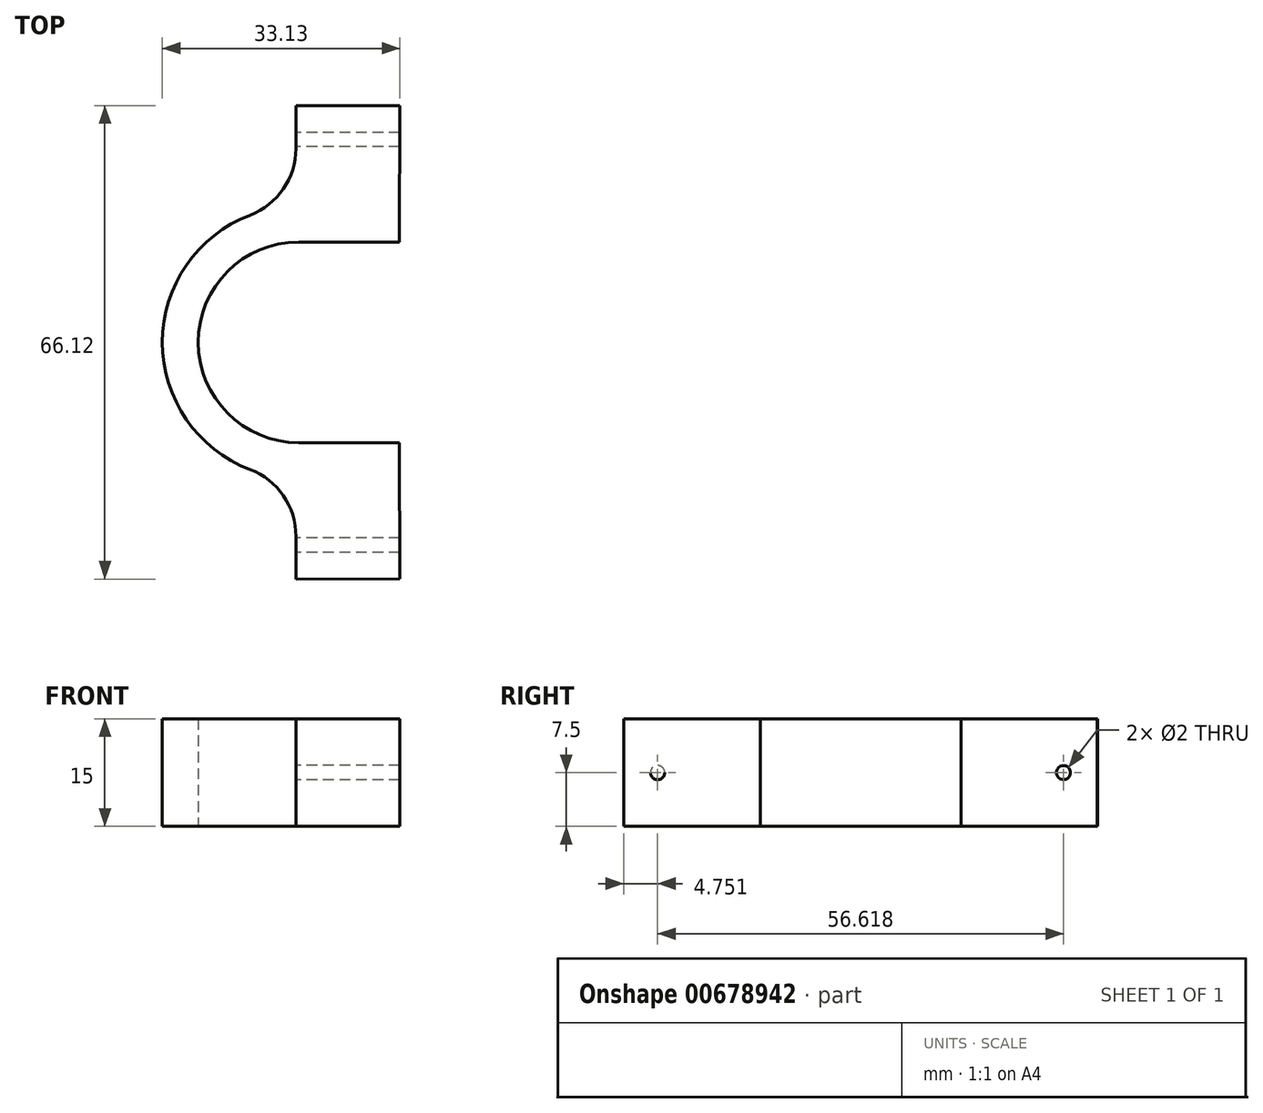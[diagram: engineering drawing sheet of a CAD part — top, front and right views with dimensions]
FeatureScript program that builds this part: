
annotation { "Feature Type Name" : "Feature", "Feature Type Description" : "" }
export const myFeature = defineFeature(function(context is Context, id is Id, definition is map)
    precondition{}
    {
        {
            var Q0;
            Q0=qCreatedBy(makeId("Top.planeOp"),FACE);
            var sketch = newSketch(context, id + "F0", { "sketchPlane" : qUnion([Q0])});
            skLineSegment(sketch, "E0.top", {"start": v(0, 0) * mm, "end": v(14, 0) * mm});
            skLineSegment(sketch, "E0.right", {"start": v(14.13, 33) * mm, "end": v(14.05, 14) * mm});
            skArc(sketch, "E1", {"start": v(0, 14) * mm, "mid": v(-9.9, 9.9) * mm, "end": v(-14, 0) * mm});
            skLineSegment(sketch, "E2.0", {"start": v(-0.36, 33.06) * mm, "end": v(-0.36, 19) * mm});
            skLineSegment(sketch, "E2.1", {"start": v(-0.36, 33.06) * mm, "end": v(14.13, 33) * mm});
            skArc(sketch, "E3.trimOffspring", {"start": v(-0.36, 19) * mm, "mid": v(-13.56, 13.3) * mm, "end": v(-19, 0) * mm});
            skLineSegment(sketch, "E4", {"start": v(0, 14) * mm, "end": v(14.05, 14) * mm});
            skLineSegment(sketch, "E5", {"start": v(0, 0) * mm, "end": v(-52.17, 0) * mm});
            skLineSegment(sketch, "E6.MirrorCS", {"start": v(0, -14) * mm, "end": v(14.05, -14) * mm});
            skArc(sketch, "E7.MirrorCS", {"start": v(0, -14) * mm, "mid": v(-9.9, -9.9) * mm, "end": v(-14, 0) * mm});
            skArc(sketch, "E8.MirrorCS", {"start": v(-0.36, -19) * mm, "mid": v(-13.56, -13.3) * mm, "end": v(-19, 0) * mm});
            skLineSegment(sketch, "E9.MirrorCS", {"start": v(-0.36, -33.06) * mm, "end": v(-0.36, -19) * mm});
            skLineSegment(sketch, "E10.MirrorCS", {"start": v(-0.36, -33.06) * mm, "end": v(14.13, -33) * mm});
            skLineSegment(sketch, "E11.MirrorCS", {"start": v(14.13, -33) * mm, "end": v(14.05, -14) * mm});
            skLineSegment(sketch, "E12", {"start": v(14.05, -14) * mm, "end": v(14, 0) * mm});
            skLineSegment(sketch, "E13", {"start": v(14.05, 14) * mm, "end": v(14, 0) * mm});
            skSolve(sketch);
        }
        {
            var Q0;
            Q0=makeQuery(id+"F0.imprint","IMPRINT",FACE,{"disambiguationData":[TD([[makeQuery(id+"F0.imprint","IMPRINT",EDGE,{"derivedFrom":sQuery(id+"F0.wireOp",EDGE,"E0.right")}),-1.0]])]});
            var Q1;
            Q1=makeQuery(id+"F0.imprint","IMPRINT",FACE,{"disambiguationData":[TD([[makeQuery(id+"F0.imprint","IMPRINT",EDGE,{"derivedFrom":sQuery(id+"F0.wireOp",EDGE,"E6.MirrorCS")}),-1.0]])]});
            extrude(context, id + "F1", {"entities" : qUnion([Q0, Q1]), "depth" : 15 * mm, "offsetDistance" : 25 * mm});
        }
        {
            var Q0;
            Q0=makeQuery(id+"F1.opExtrude","SWEPT_EDGE",EDGE,{"disambiguationData":[OSD([sQuery(id+"F0.wireOp",EDGE,"E2.0"),sQuery(id+"F0.wireOp",EDGE,"E3.trimOffspring")])]});
            var Q1;
            Q1=makeQuery(id+"F1.opExtrude","SWEPT_EDGE",EDGE,{"disambiguationData":[OSD([sQuery(id+"F0.wireOp",EDGE,"E8.MirrorCS"),sQuery(id+"F0.wireOp",EDGE,"E9.MirrorCS")])]});
            fillet(context, id + "F2", {"entities" : qUnion([Q0, Q1]), "radius" : 10 * mm, "tangentPropagation" : true, "allowEdgeOverflow" : false});
        }
        {
            var Q0;
            Q0=makeQuery(id+"F1.opExtrude","SWEPT_FACE",FACE,{"disambiguationData":[OSD([sQuery(id+"F0.wireOp",EDGE,"E2.0")])]});
            var sketch = newSketch(context, id + "F3", { "sketchPlane" : qUnion([Q0])});
            skPoint(sketch, "E14", {"position": v(-28.3, 7.5) * mm});
            skPoint(sketch, "E14.positionSnap0", {"position": v(-33.06, 7.5) * mm});
            skLineSegment(sketch, "E15", {"start": v(0, 0) * mm, "end": v(0, 9.4) * mm});
            skPoint(sketch, "E16.MirrorP", {"position": v(28.3, 7.5) * mm});
            skSolve(sketch);
        }
        {
            var Q0;
            Q0=sQuery(id+"F3.wireOp",VERTEX,"E14");
            var Q1;
            Q1=sQuery(id+"F3.wireOp",VERTEX,"E16.MirrorP");
            var Q2;
            Q2=makeQuery(id+"F1.opExtrude","SWEPT_BODY",BODY,{"disambiguationData":[OSD([sQuery(id+"F0.wireOp",EDGE,"E0.right"),sQuery(id+"F0.wireOp",EDGE,"E1"),sQuery(id+"F0.wireOp",EDGE,"E2.0"),sQuery(id+"F0.wireOp",EDGE,"E2.1"),sQuery(id+"F0.wireOp",EDGE,"E3.trimOffspring"),sQuery(id+"F0.wireOp",EDGE,"E4"),sQuery(id+"F0.wireOp",EDGE,"E6.MirrorCS"),sQuery(id+"F0.wireOp",EDGE,"E7.MirrorCS"),sQuery(id+"F0.wireOp",EDGE,"E8.MirrorCS"),sQuery(id+"F0.wireOp",EDGE,"E9.MirrorCS"),sQuery(id+"F0.wireOp",EDGE,"E10.MirrorCS"),sQuery(id+"F0.wireOp",EDGE,"E11.MirrorCS")])]});
            hole(context, id + "F4", {"style" : HoleStyle.SIMPLE, "endStyle" : HoleEndStyle.THROUGH, "holeDiameter" : 2 * mm, "majorDiameter" : 5 * mm, "isTappedThrough" : true, "tappedDepth" : 12 * mm, "tapClearance" : 3, "locations" : qUnion([Q0, Q1]), "scope" : qUnion([Q2])});
        }
    });
